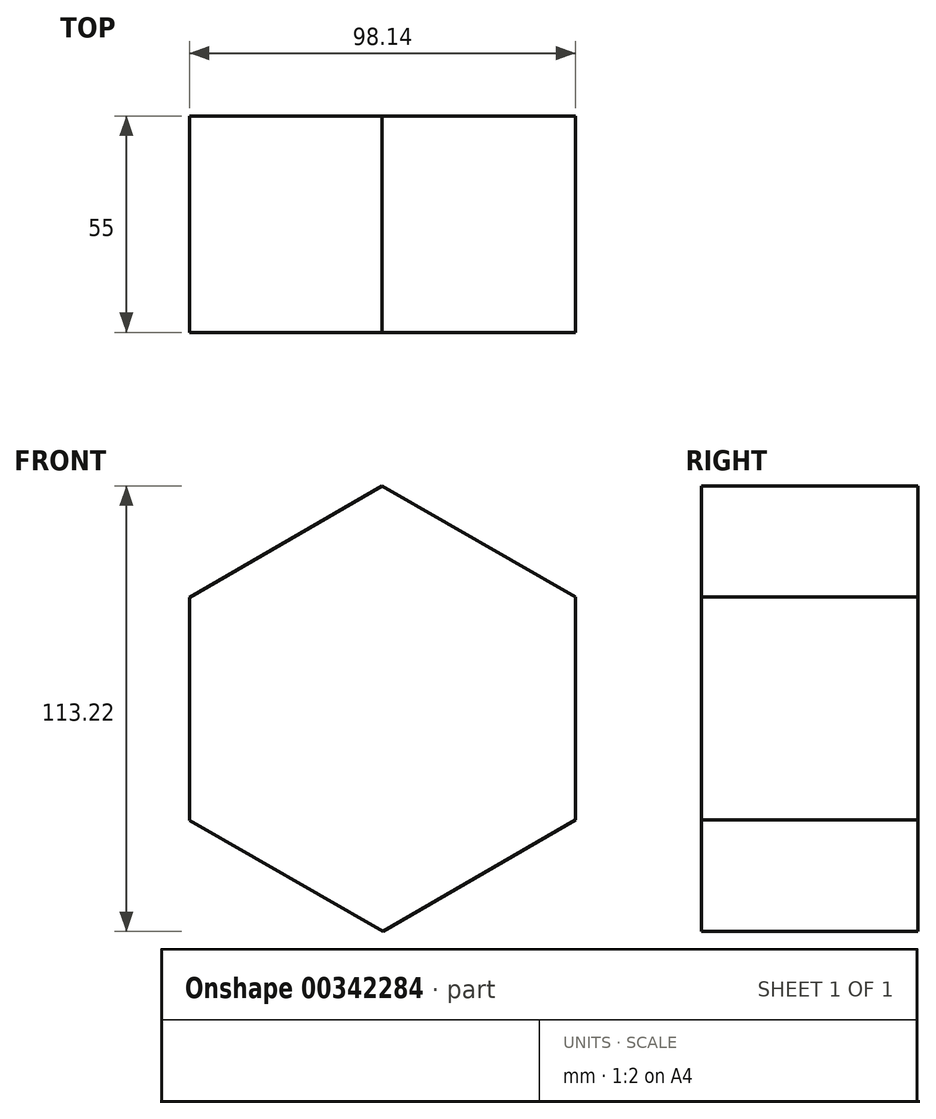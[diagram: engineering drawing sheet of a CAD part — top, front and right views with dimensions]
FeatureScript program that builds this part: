
annotation { "Feature Type Name" : "Feature", "Feature Type Description" : "" }
export const myFeature = defineFeature(function(context is Context, id is Id, definition is map)
    precondition{}
    {
        {
            var Q0;
            Q0=qCreatedBy(makeId("Front.planeOp"),FACE);
            var sketch = newSketch(context, id + "F0", { "sketchPlane" : qUnion([Q0])});
            skCircle(sketch, "E0.cCircle", {"center": v(0, 0) * mm, "radius": 49.03 * mm, "construction": true});
            skLineSegment(sketch, "E0.0", {"start": v(-0.09, 56.61) * mm, "end": v(48.98, 28.38) * mm});
            skLineSegment(sketch, "E0.1", {"start": v(48.98, 28.38) * mm, "end": v(49.07, -28.23) * mm});
            skLineSegment(sketch, "E0.2", {"start": v(49.07, -28.23) * mm, "end": v(0.09, -56.61) * mm});
            skLineSegment(sketch, "E0.3", {"start": v(0.09, -56.61) * mm, "end": v(-48.98, -28.38) * mm});
            skLineSegment(sketch, "E0.4", {"start": v(-48.98, -28.38) * mm, "end": v(-49.07, 28.23) * mm});
            skLineSegment(sketch, "E0.5", {"start": v(-49.07, 28.23) * mm, "end": v(-0.09, 56.61) * mm});
            skPoint(sketch, "E0.0.midPoint", {"position": v(24.45, 42.5) * mm});
            skCircle(sketch, "E1.1.0.0", {"center": v(99.9, 4.31) * mm, "radius": 49.03 * mm, "construction": true});
            skCircle(sketch, "E1.2.0.0", {"center": v(199.81, 8.63) * mm, "radius": 49.03 * mm, "construction": true});
            skLineSegment(sketch, "E1.direction1", {"start": v(0, 0) * mm, "end": v(99.9, 4.31) * mm, "construction": true});
            skSolve(sketch);
        }
        {
            var Q0;
            Q0 = qSketchRegion(id + "F0", true);
            extrude(context, id + "F1", {"entities" : qUnion([Q0]), "depth" : 55 * mm});
        }
    });
